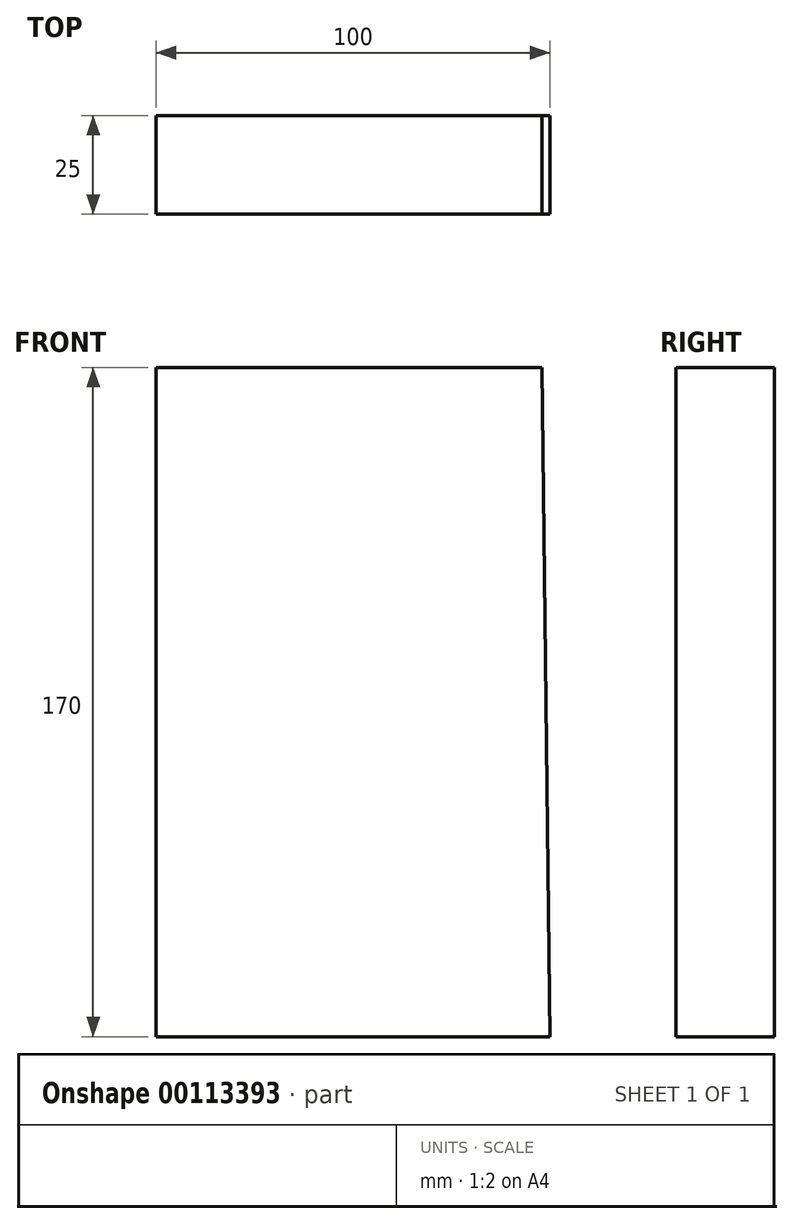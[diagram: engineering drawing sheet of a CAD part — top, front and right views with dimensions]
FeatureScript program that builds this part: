
annotation { "Feature Type Name" : "Feature", "Feature Type Description" : "" }
export const myFeature = defineFeature(function(context is Context, id is Id, definition is map)
    precondition{}
    {
        {
            var Q0;
            Q0=qCreatedBy(makeId("Front.planeOp"),FACE);
            var sketch = newSketch(context, id + "F0", { "sketchPlane" : qUnion([Q0])});
            skLineSegment(sketch, "E0", {"start": v(0, 0) * mm, "end": v(0, 170) * mm});
            skLineSegment(sketch, "E1", {"start": v(0, 170) * mm, "end": v(98, 170) * mm});
            skLineSegment(sketch, "E2", {"start": v(0, 0) * mm, "end": v(100, 0) * mm});
            skLineSegment(sketch, "E3", {"start": v(98, 170) * mm, "end": v(100, 0) * mm});
            skSolve(sketch);
        }
        {
            var Q0;
            Q0 = qSketchRegion(id + "F0", true);
            extrude(context, id + "F1", {"entities" : qUnion([Q0]), "depth" : 25 * mm});
        }
    });
